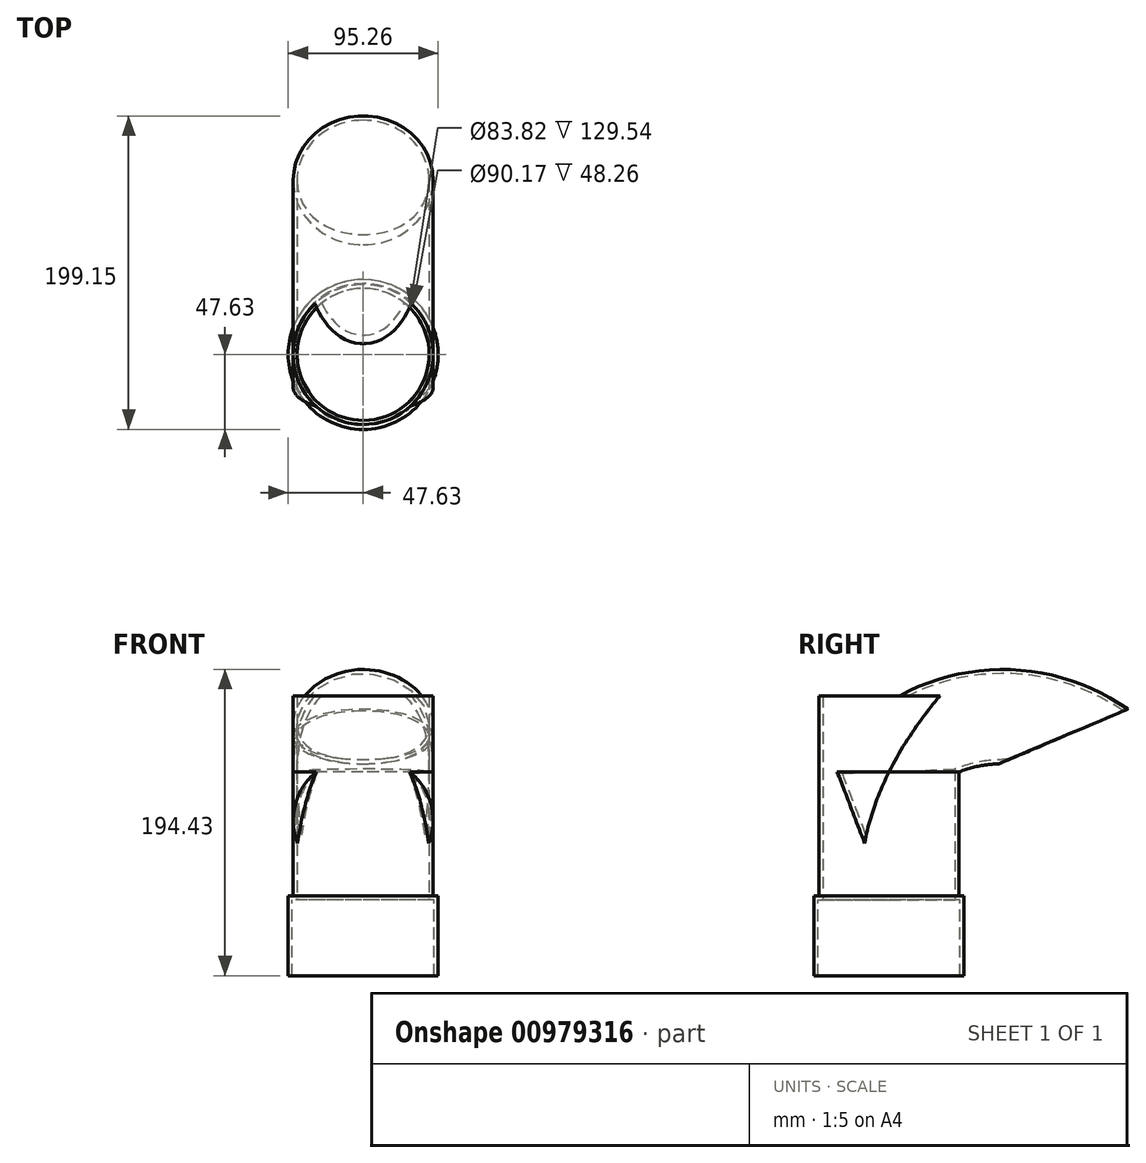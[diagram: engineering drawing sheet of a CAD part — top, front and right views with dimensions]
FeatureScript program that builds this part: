
annotation { "Feature Type Name" : "Feature", "Feature Type Description" : "" }
export const myFeature = defineFeature(function(context is Context, id is Id, definition is map)
    precondition{}
    {
        {
            var Q0;
            Q0=qCreatedBy(makeId("Top.planeOp"),FACE);
            var sketch = newSketch(context, id + "F0", { "sketchPlane" : qUnion([Q0])});
            skCircle(sketch, "E0", {"center": v(0, 0) * mm, "radius": 44.45 * mm});
            skSolve(sketch);
        }
        {
            var Q0;
            Q0=makeQuery(id+"F0.imprint","IMPRINT",FACE,{"disambiguationData":[TD([[makeQuery(id+"F0.imprint","IMPRINT",EDGE,{"derivedFrom":sQuery(id+"F0.wireOp",EDGE,"E0")}),1.0]])]});
            extrude(context, id + "F1", {"entities" : qUnion([Q0]), "depth" : 127 * mm, "offsetDistance" : 25.4 * mm});
        }
        {
            var Q0;
            Q0=qCreatedBy(makeId("Right.planeOp"),FACE);
            var sketch = newSketch(context, id + "F2", { "sketchPlane" : qUnion([Q0])});
            skLineSegment(sketch, "E1", {"start": v(0, 6.35) * mm, "end": v(69.85, 6.35) * mm, "construction": true});
            skArc(sketch, "E2", {"start": v(0, 6.35) * mm, "mid": v(20.32, 56.6) * mm, "end": v(69.85, 78.6) * mm});
            skSolve(sketch);
        }
        {
            var Q0;
            Q0=sQuery(id+"F2.wireOp",VERTEX,"E2.end");
            var Q1;
            Q1=qCreatedBy(makeId("Front.planeOp"),FACE);
            cPlane(context, id + "F3", {"entities" : qUnion([Q0, Q1]), "cplaneType" : CPlaneType.PLANE_POINT, "offset" : 25.4 * mm, "width" : 152.4 * mm, "height" : 152.4 * mm});
        }
        {
            var Q0;
            Q0=qCreatedBy(id+"F3.planeOp",FACE);
            var sketch = newSketch(context, id + "F4", { "sketchPlane" : qUnion([Q0])});
            skCircle(sketch, "E3", {"center": v(0, 78.6) * mm, "radius": 44.45 * mm});
            skSolve(sketch);
        }
        {
            var Q0;
            Q0=makeQuery(id+"F4.imprint","IMPRINT",FACE,{"disambiguationData":[TD([[makeQuery(id+"F4.imprint","IMPRINT",EDGE,{"derivedFrom":sQuery(id+"F4.wireOp",EDGE,"E3")}),1.0]])]});
            var Q1;
            Q1=sQuery(id+"F2.wireOp",EDGE,"E2");
            sweep(context, id + "F5", {"operationType" : NewBodyOperationType.ADD, "profiles" : qUnion([Q0]), "path" : qUnion([Q1])});
        }
        {
            var Q0;
            Q0=makeQuery(id+"F1.opExtrude","CAP_FACE",FACE,{"disambiguationData":[OSD([sQuery(id+"F0.wireOp",EDGE,"E0")])],"isStart":true});
            var Q1;
            Q1=makeQuery(id+"F5.opSweep","CAP_FACE",FACE,{"disambiguationData":[OSD([sQuery(id+"F2.wireOp",VERTEX,"E2.end"),sQuery(id+"F4.wireOp",EDGE,"E3")])],"isStart":true});
            var Q2;
            Q2=makeQuery(id+"F1.opExtrude","CAP_FACE",FACE,{"disambiguationData":[OSD([sQuery(id+"F0.wireOp",EDGE,"E0")])],"isStart":false});
            shell(context, id + "F6", {"entities" : qUnion([Q0, Q1, Q2]), "thickness" : 2.54 * mm});
        }
        {
            var Q0;
            Q0=qCreatedBy(makeId("Top.planeOp"),FACE);
            var sketch = newSketch(context, id + "F7", { "sketchPlane" : qUnion([Q0])});
            skCircle(sketch, "E4", {"center": v(0, 0) * mm, "radius": 47.63 * mm});
            skSolve(sketch);
        }
        {
            var Q0;
            Q0=makeQuery(id+"F7.imprint","IMPRINT",FACE,{"disambiguationData":[TD([[makeQuery(id+"F7.imprint","IMPRINT",EDGE,{"derivedFrom":sQuery(id+"F7.wireOp",EDGE,"E4")}),1.0]])]});
            extrude(context, id + "F8", {"entities" : qUnion([Q0]), "operationType" : NewBodyOperationType.ADD, "oppositeDirection" : true, "depth" : 50.8 * mm, "offsetDistance" : 25.4 * mm});
        }
        {
            var Q0;
            Q0=makeQuery(id+"F8.opExtrude","CAP_FACE",FACE,{"disambiguationData":[OSD([sQuery(id+"F7.wireOp",EDGE,"E4")])],"isStart":false});
            var Q1;
            Q1=makeQuery(id+"F8.boolean.opBoolean","SPLIT",FACE,{"disambiguationData":[TD([makeQuery(id+"F6.opShell","OFFSET_FACE",FACE,{"disambiguationData":[OSD([sQuery(id+"F0.wireOp",EDGE,"E0")])]})])],"derivedFrom":makeQuery(id+"F8.opExtrude","CAP_FACE",FACE,{"disambiguationData":[OSD([sQuery(id+"F7.wireOp",EDGE,"E4")])],"isStart":true})});
            shell(context, id + "F9", {"entities" : qUnion([Q0, Q1]), "thickness" : 2.54 * mm});
        }
    });
